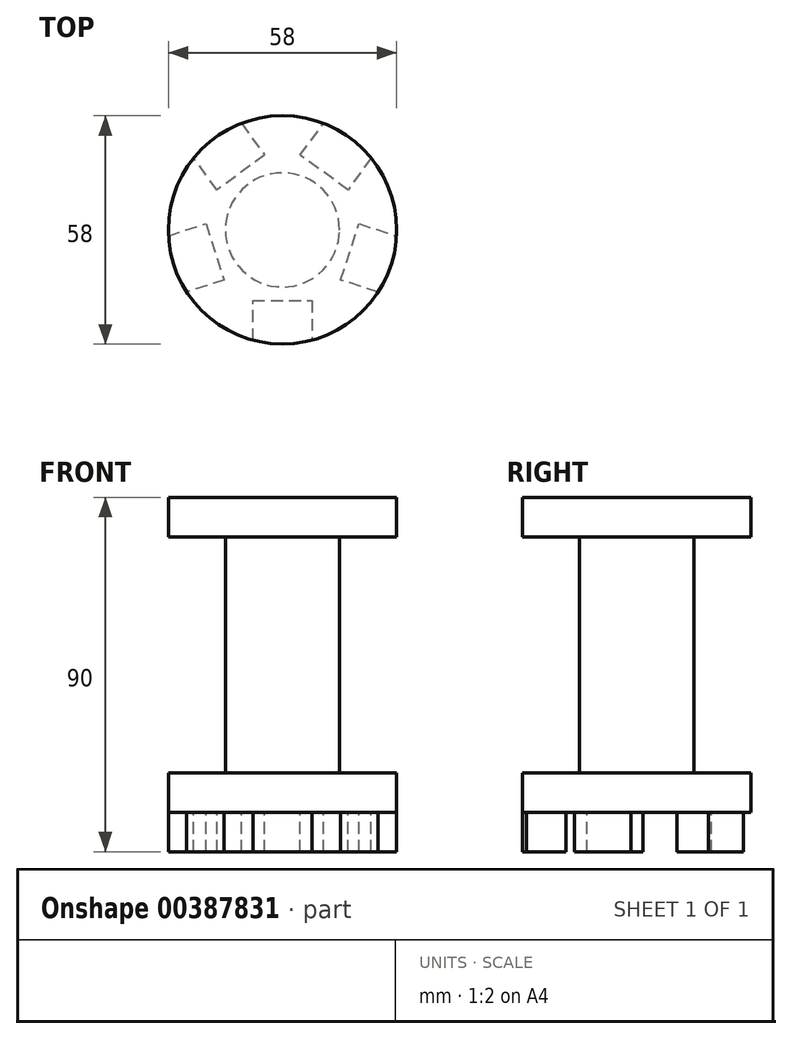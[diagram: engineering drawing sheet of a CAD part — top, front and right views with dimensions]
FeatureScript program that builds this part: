
annotation { "Feature Type Name" : "Feature", "Feature Type Description" : "" }
export const myFeature = defineFeature(function(context is Context, id is Id, definition is map)
    precondition{}
    {
        {
            var Q0;
            Q0=qCreatedBy(makeId("Front.planeOp"),FACE);
            var sketch = newSketch(context, id + "F0", { "sketchPlane" : qUnion([Q0])});
            skLineSegment(sketch, "E0", {"start": v(0, 69.7) * mm, "end": v(0, -67.6) * mm, "construction": true});
            skLineSegment(sketch, "E1.bottom", {"start": v(0, 23.74) * mm, "end": v(29, 23.74) * mm, "construction": true});
            skLineSegment(sketch, "E1.left", {"start": v(0, 23.74) * mm, "end": v(0, 13.74) * mm, "construction": true});
            skLineSegment(sketch, "E1.right", {"start": v(29, 23.74) * mm, "end": v(29, 13.74) * mm, "construction": true});
            skPoint(sketch, "E2.oppositeSnap0", {"position": v(14.5, 13.74) * mm});
            skLineSegment(sketch, "E2.left", {"start": v(0, 13.74) * mm, "end": v(0, -46.26) * mm, "construction": true});
            skLineSegment(sketch, "E2.right", {"start": v(14.5, 13.74) * mm, "end": v(14.5, -46.26) * mm, "construction": true});
            skLineSegment(sketch, "E3.top", {"start": v(0, -56.26) * mm, "end": v(29, -56.26) * mm, "construction": true});
            skLineSegment(sketch, "E3.left", {"start": v(0, -46.26) * mm, "end": v(0, -56.26) * mm, "construction": true});
            skLineSegment(sketch, "E3.right", {"start": v(29, -46.26) * mm, "end": v(29, -56.26) * mm, "construction": true});
            skLineSegment(sketch, "E4", {"start": v(0, 23.74) * mm, "end": v(29, 23.74) * mm});
            skLineSegment(sketch, "E5", {"start": v(29, 13.74) * mm, "end": v(29, 23.74) * mm});
            skLineSegment(sketch, "E6", {"start": v(29, 13.74) * mm, "end": v(14.5, 13.74) * mm});
            skLineSegment(sketch, "E7", {"start": v(14.5, 13.74) * mm, "end": v(14.5, -46.26) * mm});
            skLineSegment(sketch, "E8", {"start": v(14.5, -46.26) * mm, "end": v(29, -46.26) * mm});
            skLineSegment(sketch, "E9", {"start": v(29, -46.26) * mm, "end": v(29, -56.26) * mm});
            skLineSegment(sketch, "E10", {"start": v(29, -56.26) * mm, "end": v(0, -56.26) * mm});
            skLineSegment(sketch, "E11", {"start": v(0, -56.26) * mm, "end": v(0, 23.74) * mm});
            skSolve(sketch);
        }
        {
            var Q0;
            Q0=makeQuery(id+"F0.imprint","IMPRINT",FACE,{"disambiguationData":[TD([[makeQuery(id+"F0.imprint","IMPRINT",EDGE,{"derivedFrom":sQuery(id+"F0.wireOp",EDGE,"E4")}),-1.0]])]});
            var Q1;
            Q1=sQuery(id+"F0.wireOp",EDGE,"E11");
            revolve(context, id + "F1", {"entities" : qUnion([Q0]), "axis" : qUnion([Q1]), "revolveType" : RevolveType.FULL});
        }
        {
            var Q0;
            Q0=makeQuery(id+"F1.opRevolve","SWEPT_FACE",FACE,{"disambiguationData":[OSD([sQuery(id+"F0.wireOp",EDGE,"E10")])]});
            var sketch = newSketch(context, id + "F2", { "sketchPlane" : qUnion([Q0])});
            skLineSegment(sketch, "E12", {"start": v(-7.5, 28.01) * mm, "end": v(-7.5, 18.01) * mm});
            skLineSegment(sketch, "E13", {"start": v(-7.5, 18.01) * mm, "end": v(7.5, 18.01) * mm});
            skLineSegment(sketch, "E14", {"start": v(7.5, 18.01) * mm, "end": v(7.5, 28.01) * mm});
            skSolve(sketch);
        }
        {
            var Q0;
            {var subQ0=sQuery(id+"F2.wireOp",EDGE,"E12");Q0=makeQuery(id+"F2.imprint","IMPRINT",FACE,{"disambiguationData":[TD([[makeQuery(id+"F2.imprint","IMPRINT",EDGE,{"derivedFrom":subQ0}),1.0]])]});}
            extrude(context, id + "F3", {"entities" : qUnion([Q0]), "operationType" : NewBodyOperationType.ADD, "depth" : 10 * mm});
        }
        {
            var Q0;
            Q0=makeQuery(id+"F1.opRevolve","SWEPT_BODY",BODY,{"disambiguationData":[OSD([sQuery(id+"F0.wireOp",EDGE,"E4"),sQuery(id+"F0.wireOp",EDGE,"E5"),sQuery(id+"F0.wireOp",EDGE,"E6"),sQuery(id+"F0.wireOp",EDGE,"E7"),sQuery(id+"F0.wireOp",EDGE,"E8"),sQuery(id+"F0.wireOp",EDGE,"E9"),sQuery(id+"F0.wireOp",EDGE,"E10"),sQuery(id+"F0.wireOp",EDGE,"E11")])]});
            var Q1;
            Q1=makeQuery(id+"F1.opRevolve","SWEPT_FACE",FACE,{"disambiguationData":[OSD([sQuery(id+"F0.wireOp",EDGE,"E7")])]});
            circularPattern(context, id + "F4", {"entities" : qUnion([Q0]), "axis" : qUnion([Q1]), "angle" : 360 * degree, "instanceCount" : 5, "equalSpace" : true});
        }
    });
